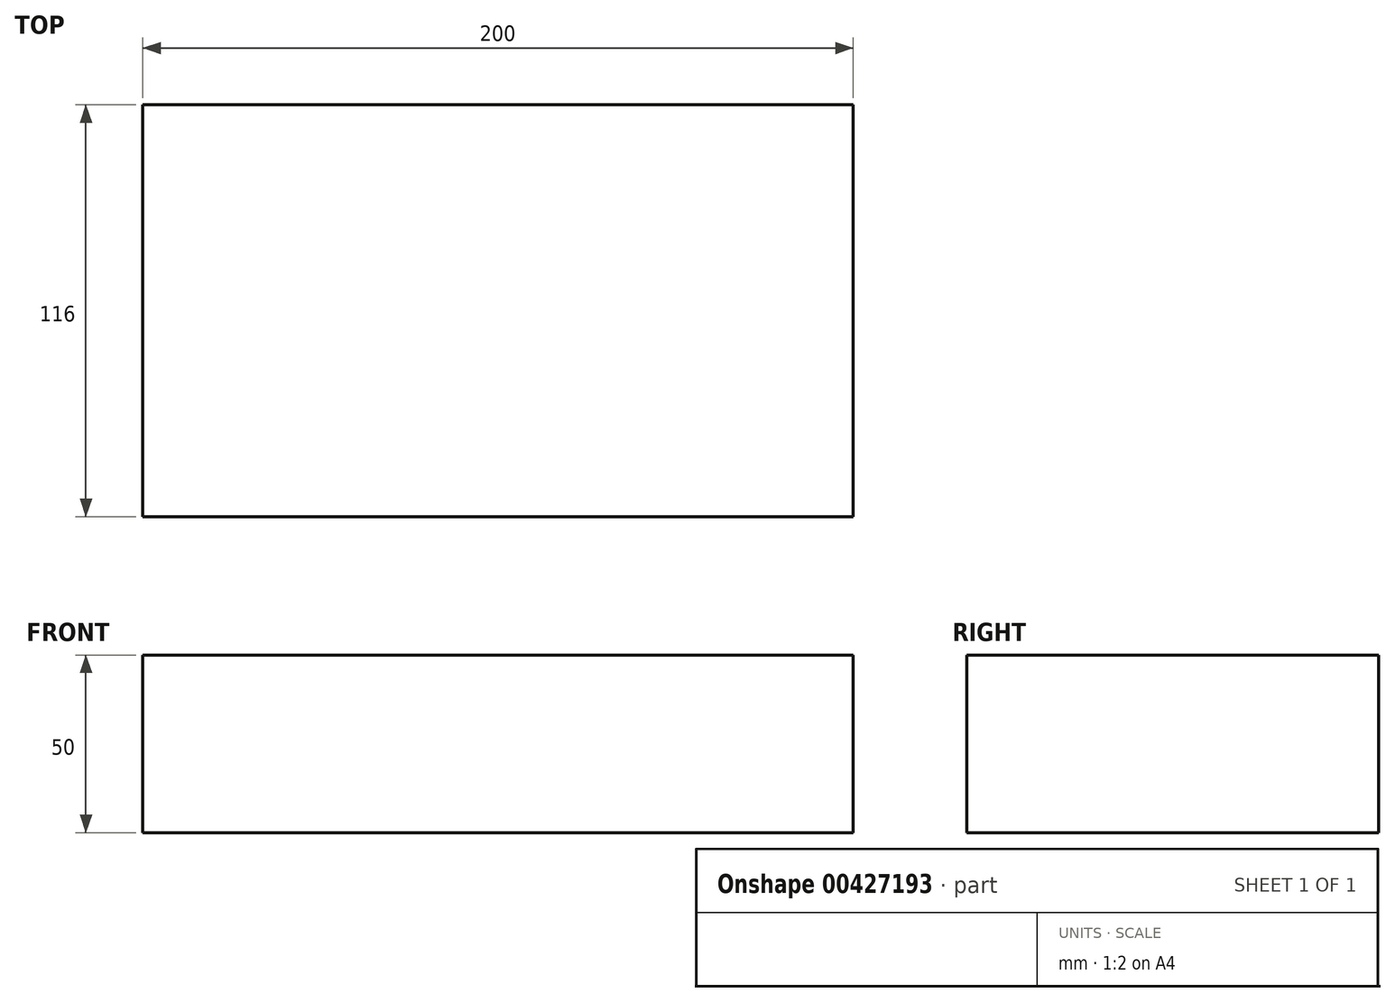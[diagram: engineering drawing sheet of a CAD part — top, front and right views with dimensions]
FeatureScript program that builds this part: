
annotation { "Feature Type Name" : "Feature", "Feature Type Description" : "" }
export const myFeature = defineFeature(function(context is Context, id is Id, definition is map)
    precondition{}
    {
        {
            var Q0;
            Q0=qCreatedBy(makeId("Top.planeOp"),FACE);
            var sketch = newSketch(context, id + "F0", { "sketchPlane" : qUnion([Q0])});
            skLineSegment(sketch, "E0.bottom", {"start": v(100, -58) * mm, "end": v(-100, -58) * mm});
            skLineSegment(sketch, "E0.top", {"start": v(100, 58) * mm, "end": v(-100, 58) * mm});
            skLineSegment(sketch, "E0.left", {"start": v(100, -58) * mm, "end": v(100, 58) * mm});
            skLineSegment(sketch, "E0.right", {"start": v(-100, -58) * mm, "end": v(-100, 58) * mm});
            skPoint(sketch, "E0.middle", {"position": v(0, 0) * mm});
            skSolve(sketch);
        }
        {
            var Q0;
            Q0=makeQuery(id+"F0.imprint","IMPRINT",FACE,{"disambiguationData":[TD([[makeQuery(id+"F0.imprint","IMPRINT",EDGE,{"derivedFrom":sQuery(id+"F0.wireOp",EDGE,"E0.bottom")}),-1.0]])]});
            extrude(context, id + "F1", {"entities" : qUnion([Q0]), "oppositeDirection" : true, "depth" : 50 * mm});
        }
    });
